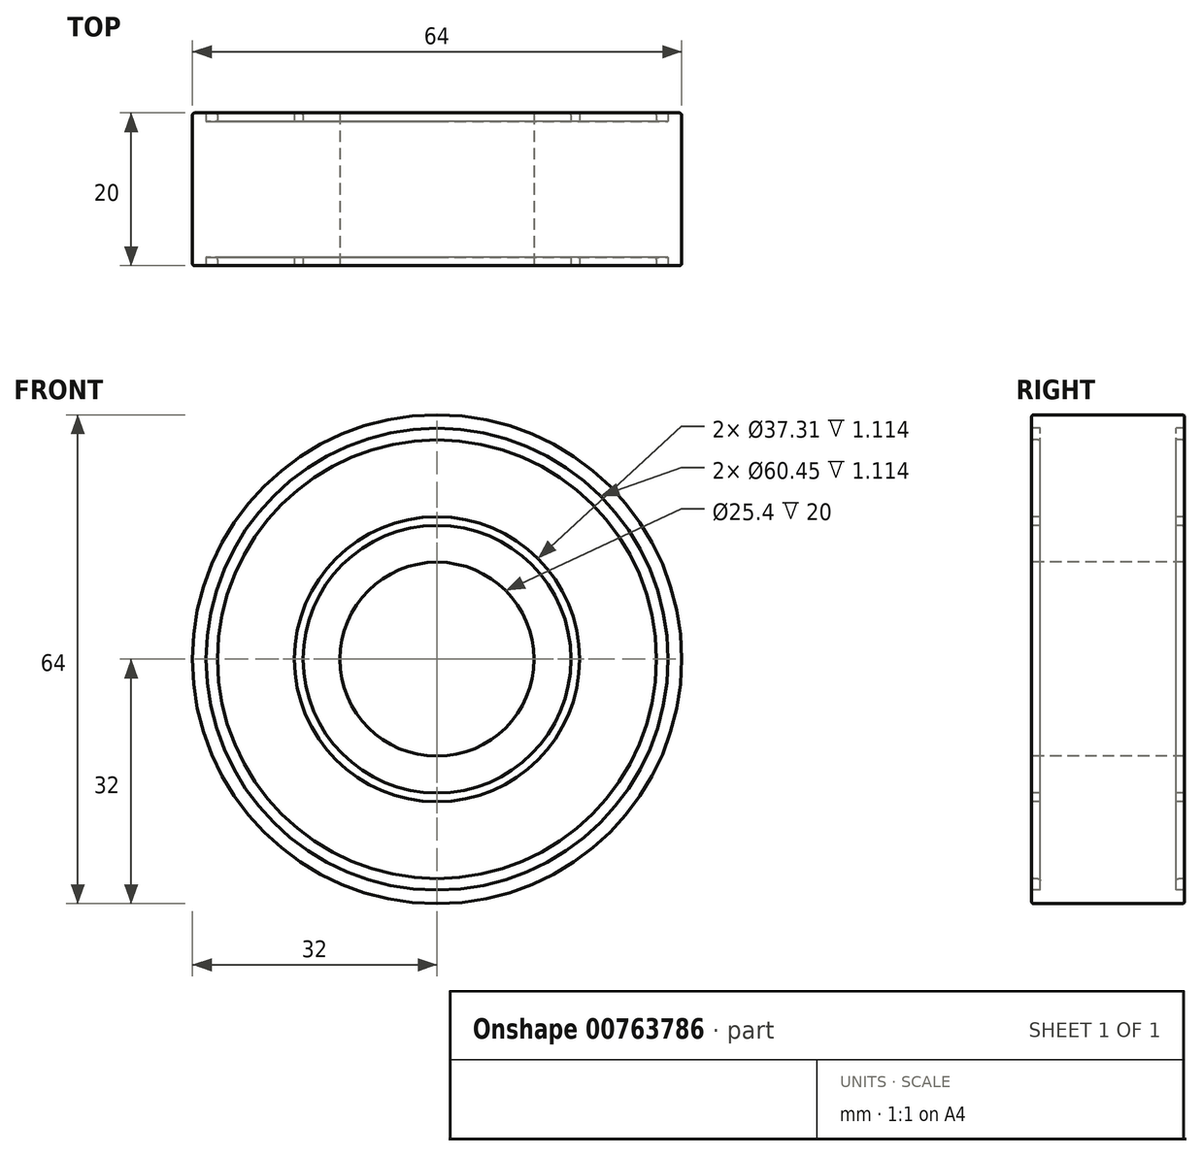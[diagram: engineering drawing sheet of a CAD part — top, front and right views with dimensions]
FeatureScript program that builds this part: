
annotation { "Feature Type Name" : "Feature", "Feature Type Description" : "" }
export const myFeature = defineFeature(function(context is Context, id is Id, definition is map)
    precondition{}
    {
        {
            var Q0;
            Q0=qCreatedBy(makeId("Right.planeOp"),FACE);
            var sketch = newSketch(context, id + "F0", { "sketchPlane" : qUnion([Q0])});
            skLineSegment(sketch, "E0", {"start": v(0, 0) * mm, "end": v(0, 12.7) * mm, "construction": true});
            skLineSegment(sketch, "E1", {"start": v(0, 12.7) * mm, "end": v(-10, 12.7) * mm});
            skLineSegment(sketch, "E2", {"start": v(-10, 12.7) * mm, "end": v(-10, 17.22) * mm});
            skLineSegment(sketch, "E3", {"start": v(-9.7, 17.52) * mm, "end": v(-8.89, 17.52) * mm});
            skLineSegment(sketch, "E4", {"start": v(-8.89, 17.52) * mm, "end": v(-8.89, 18.66) * mm});
            skLineSegment(sketch, "E5", {"start": v(-8.89, 18.66) * mm, "end": v(-10, 18.66) * mm});
            skLineSegment(sketch, "E6", {"start": v(-10, 18.66) * mm, "end": v(-10, 28.4) * mm});
            skLineSegment(sketch, "E7", {"start": v(-9.7, 28.7) * mm, "end": v(-9.19, 28.7) * mm});
            skLineSegment(sketch, "E8", {"start": v(-8.89, 29) * mm, "end": v(-8.89, 30.23) * mm});
            skLineSegment(sketch, "E9", {"start": v(-8.89, 30.23) * mm, "end": v(-10, 30.23) * mm});
            skLineSegment(sketch, "E10", {"start": v(-10, 30.23) * mm, "end": v(-10, 31.7) * mm});
            skLineSegment(sketch, "E11", {"start": v(-9.7, 32) * mm, "end": v(0, 32) * mm});
            skPoint(sketch, "E12.visualSharp", {"position": v(-8.89, 28.7) * mm});
            skArc(sketch, "E12.filletArc", {"start": v(-9.19, 28.7) * mm, "mid": v(-8.97, 28.8) * mm, "end": v(-8.89, 29) * mm});
            skPoint(sketch, "E13.visualSharp", {"position": v(-10, 28.7) * mm});
            skArc(sketch, "E13.filletArc", {"start": v(-9.7, 28.7) * mm, "mid": v(-9.91, 28.62) * mm, "end": v(-10, 28.4) * mm});
            skPoint(sketch, "E14.visualSharp", {"position": v(-10, 17.52) * mm});
            skArc(sketch, "E14.filletArc", {"start": v(-9.7, 17.52) * mm, "mid": v(-9.91, 17.43) * mm, "end": v(-10, 17.22) * mm});
            skPoint(sketch, "E15.visualSharp", {"position": v(-10, 32) * mm});
            skArc(sketch, "E15.filletArc", {"start": v(-9.7, 32) * mm, "mid": v(-9.91, 31.91) * mm, "end": v(-10, 31.7) * mm});
            skLineSegment(sketch, "E16.MirrorCS", {"start": v(9.7, 32) * mm, "end": v(0, 32) * mm});
            skLineSegment(sketch, "E17.MirrorCS", {"start": v(10, 30.23) * mm, "end": v(10, 31.7) * mm});
            skArc(sketch, "E18.MirrorCS", {"start": v(9.7, 32) * mm, "mid": v(9.91, 31.91) * mm, "end": v(10, 31.7) * mm});
            skLineSegment(sketch, "E19.MirrorCS", {"start": v(8.89, 30.23) * mm, "end": v(10, 30.23) * mm});
            skLineSegment(sketch, "E20.MirrorCS", {"start": v(8.89, 29) * mm, "end": v(8.89, 30.23) * mm});
            skArc(sketch, "E21.MirrorCS", {"start": v(9.19, 28.7) * mm, "mid": v(8.97, 28.8) * mm, "end": v(8.89, 29) * mm});
            skLineSegment(sketch, "E22.MirrorCS", {"start": v(9.7, 28.7) * mm, "end": v(9.19, 28.7) * mm});
            skArc(sketch, "E23.MirrorCS", {"start": v(9.7, 28.7) * mm, "mid": v(9.91, 28.62) * mm, "end": v(10, 28.4) * mm});
            skLineSegment(sketch, "E24.MirrorCS", {"start": v(10, 18.66) * mm, "end": v(10, 28.4) * mm});
            skLineSegment(sketch, "E25.MirrorCS", {"start": v(8.89, 18.66) * mm, "end": v(10, 18.66) * mm});
            skLineSegment(sketch, "E26.MirrorCS", {"start": v(8.89, 17.52) * mm, "end": v(8.89, 18.66) * mm});
            skLineSegment(sketch, "E27.MirrorCS", {"start": v(9.7, 17.52) * mm, "end": v(8.89, 17.52) * mm});
            skArc(sketch, "E28.MirrorCS", {"start": v(9.7, 17.52) * mm, "mid": v(9.91, 17.43) * mm, "end": v(10, 17.22) * mm});
            skLineSegment(sketch, "E29.MirrorCS", {"start": v(10, 12.7) * mm, "end": v(10, 17.22) * mm});
            skLineSegment(sketch, "E30.MirrorCS", {"start": v(0, 12.7) * mm, "end": v(10, 12.7) * mm});
            skSolve(sketch);
        }
        {
            var Q0;
            Q0=qCreatedBy(makeId("Top.planeOp"),FACE);
            var sketch = newSketch(context, id + "F1", { "sketchPlane" : qUnion([Q0])});
            skLineSegment(sketch, "E31", {"start": v(0, -17.64) * mm, "end": v(0, 14.02) * mm, "construction": true});
            skSolve(sketch);
        }
        {
            var Q0;
            Q0 = qSketchRegion(id + "F0", true);
            var Q1;
            Q1=sQuery(id+"F1.wireOp",EDGE,"E31");
            revolve(context, id + "F2", {"surfaceOperationType" : NewSurfaceOperationType.NEW, "entities" : qUnion([Q0]), "axis" : qUnion([Q1]), "revolveType" : RevolveType.FULL});
        }
    });
